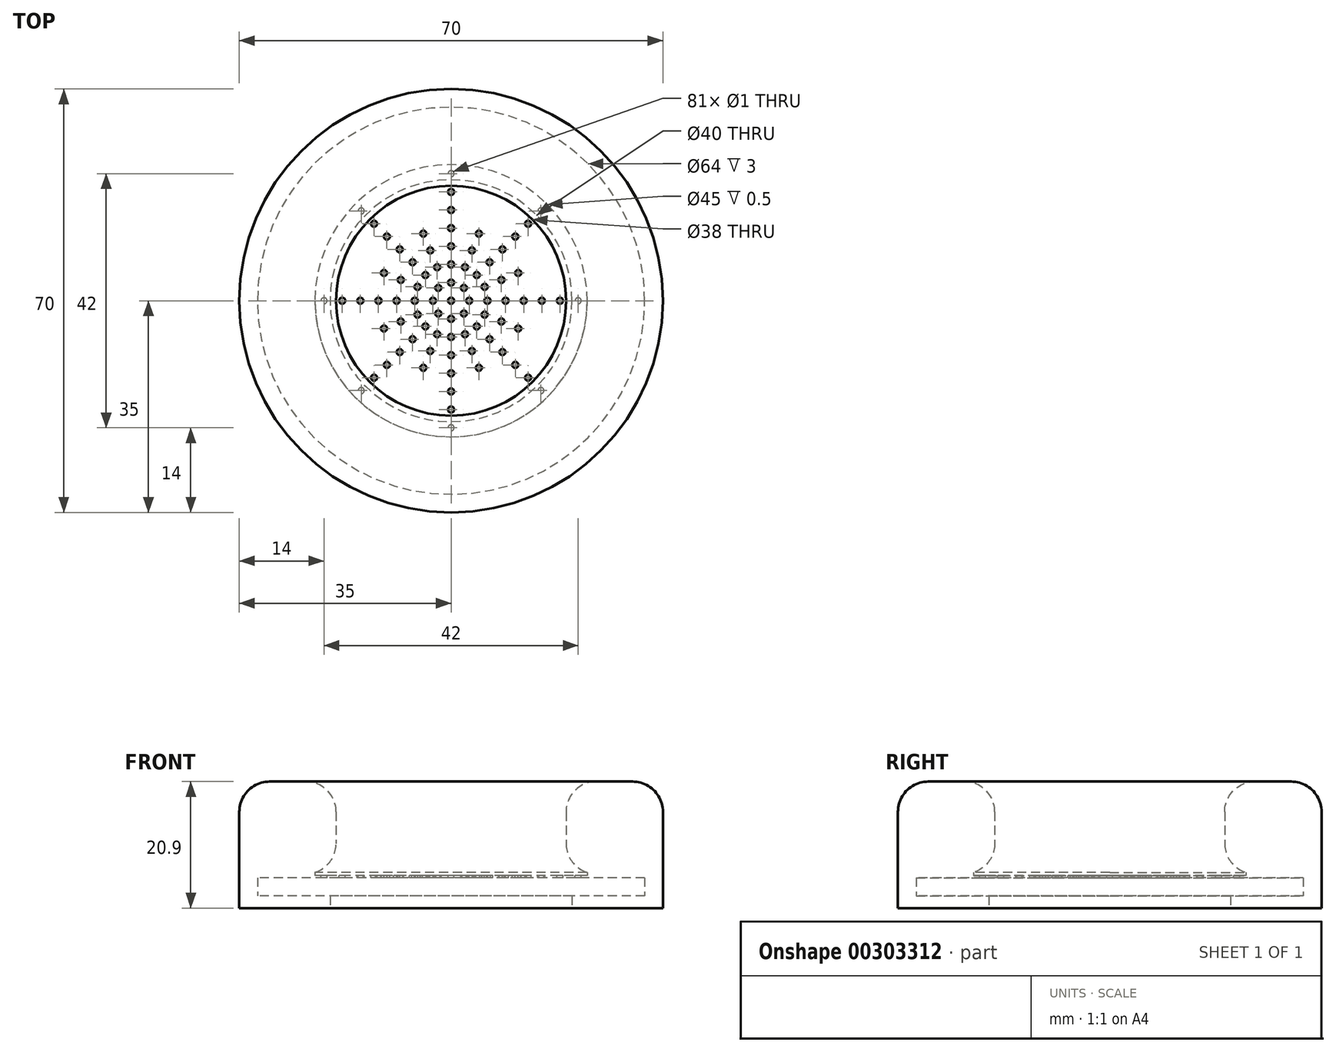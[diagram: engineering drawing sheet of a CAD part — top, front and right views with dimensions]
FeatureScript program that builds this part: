
annotation { "Feature Type Name" : "Feature", "Feature Type Description" : "" }
export const myFeature = defineFeature(function(context is Context, id is Id, definition is map)
    precondition{}
    {
        {
            var Q0;
            Q0=qCreatedBy(makeId("Top.planeOp"),FACE);
            var sketch = newSketch(context, id + "F0", { "sketchPlane" : qUnion([Q0])});
            skCircle(sketch, "E0", {"center": v(0, 0) * mm, "radius": 35 * mm});
            skCircle(sketch, "E1", {"center": v(0, 0) * mm, "radius": 20 * mm});
            skSolve(sketch);
        }
        {
            var Q0;
            Q0=makeQuery(id+"F0.imprint","IMPRINT",FACE,{"disambiguationData":[TD([[makeQuery(id+"F0.imprint","IMPRINT",EDGE,{"derivedFrom":sQuery(id+"F0.wireOp",EDGE,"E0")}),1.0]])]});
            extrude(context, id + "F1", {"entities" : qUnion([Q0]), "depth" : 2 * mm});
        }
        {
            var Q0;
            Q0=makeQuery(id+"F1.opExtrude","CAP_FACE",FACE,{"disambiguationData":[OSD([sQuery(id+"F0.wireOp",EDGE,"E0"),sQuery(id+"F0.wireOp",EDGE,"E1")])],"isStart":false});
            var sketch = newSketch(context, id + "F2", { "sketchPlane" : qUnion([Q0])});
            skCircle(sketch, "E2", {"center": v(0, 0) * mm, "radius": 32 * mm});
            skSolve(sketch);
        }
        {
            var Q0;
            Q0=makeQuery(id+"F2.imprint","IMPRINT",FACE,{"disambiguationData":[TD([[makeQuery(id+"F2.imprint","IMPRINT",EDGE,{"derivedFrom":sQuery(id+"F2.wireOp",EDGE,"E2")}),-1.0]])]});
            extrude(context, id + "F3", {"entities" : qUnion([Q0]), "operationType" : NewBodyOperationType.ADD, "depth" : 3 * mm});
        }
        {
            var Q0;
            Q0=makeQuery(id+"F3.opExtrude","CAP_FACE",FACE,{"disambiguationData":[OSD([sQuery(id+"F0.wireOp",EDGE,"E0"),sQuery(id+"F2.wireOp",EDGE,"E2")])],"isStart":false});
            var sketch = newSketch(context, id + "F4", { "sketchPlane" : qUnion([Q0])});
            skCircle(sketch, "E3", {"center": v(0, 0) * mm, "radius": 35 * mm});
            skSolve(sketch);
        }
        {
            var Q0;
            Q0 = qSketchRegion(id + "F4", true);
            extrude(context, id + "F5", {"entities" : qUnion([Q0]), "operationType" : NewBodyOperationType.ADD, "depth" : 0.4 * mm});
        }
        {
            var Q0;
            Q0=makeQuery(id+"F5.opExtrude","CAP_FACE",FACE,{"disambiguationData":[OSD([sQuery(id+"F4.wireOp",EDGE,"E3")])],"isStart":false});
            var sketch = newSketch(context, id + "F6", { "sketchPlane" : qUnion([Q0])});
            skCircle(sketch, "E4", {"center": v(0, 0) * mm, "radius": 0.5 * mm});
            skCircle(sketch, "E5.1.0.0", {"center": v(3, 0) * mm, "radius": 0.5 * mm});
            skCircle(sketch, "E5.2.0.0", {"center": v(6, 0) * mm, "radius": 0.5 * mm});
            skCircle(sketch, "E5.3.0.0", {"center": v(9, 0) * mm, "radius": 0.5 * mm});
            skCircle(sketch, "E5.4.0.0", {"center": v(12, 0) * mm, "radius": 0.5 * mm});
            skCircle(sketch, "E5.5.0.0", {"center": v(15, 0) * mm, "radius": 0.5 * mm});
            skCircle(sketch, "E5.6.0.0", {"center": v(18, 0) * mm, "radius": 0.5 * mm});
            skCircle(sketch, "E5.7.0.0", {"center": v(21, 0) * mm, "radius": 0.5 * mm});
            skLineSegment(sketch, "E5.direction1", {"start": v(0, 0) * mm, "end": v(3, 0) * mm, "construction": true});
            skCircle(sketch, "E6.1.0", {"center": v(2.12, 2.12) * mm, "radius": 0.5 * mm});
            skCircle(sketch, "E6.1.1", {"center": v(4.24, 4.24) * mm, "radius": 0.5 * mm});
            skCircle(sketch, "E6.1.2", {"center": v(6.36, 6.36) * mm, "radius": 0.5 * mm});
            skCircle(sketch, "E6.1.3", {"center": v(8.49, 8.49) * mm, "radius": 0.5 * mm});
            skCircle(sketch, "E6.1.4", {"center": v(10.6, 10.6) * mm, "radius": 0.5 * mm});
            skCircle(sketch, "E6.1.5", {"center": v(12.73, 12.73) * mm, "radius": 0.5 * mm});
            skCircle(sketch, "E6.1.6", {"center": v(14.85, 14.85) * mm, "radius": 0.5 * mm});
            skCircle(sketch, "E6.2.0", {"center": v(0, 3) * mm, "radius": 0.5 * mm});
            skCircle(sketch, "E6.2.1", {"center": v(0, 6) * mm, "radius": 0.5 * mm});
            skCircle(sketch, "E6.2.2", {"center": v(0, 9) * mm, "radius": 0.5 * mm});
            skCircle(sketch, "E6.2.3", {"center": v(0, 12) * mm, "radius": 0.5 * mm});
            skCircle(sketch, "E6.2.4", {"center": v(0, 15) * mm, "radius": 0.5 * mm});
            skCircle(sketch, "E6.2.5", {"center": v(0, 18) * mm, "radius": 0.5 * mm});
            skCircle(sketch, "E6.2.6", {"center": v(0, 21) * mm, "radius": 0.5 * mm});
            skCircle(sketch, "E6.3.0", {"center": v(-2.12, 2.12) * mm, "radius": 0.5 * mm});
            skCircle(sketch, "E6.3.1", {"center": v(-4.24, 4.24) * mm, "radius": 0.5 * mm});
            skCircle(sketch, "E6.3.2", {"center": v(-6.36, 6.36) * mm, "radius": 0.5 * mm});
            skCircle(sketch, "E6.3.3", {"center": v(-8.49, 8.49) * mm, "radius": 0.5 * mm});
            skCircle(sketch, "E6.3.4", {"center": v(-10.6, 10.6) * mm, "radius": 0.5 * mm});
            skCircle(sketch, "E6.3.5", {"center": v(-12.73, 12.73) * mm, "radius": 0.5 * mm});
            skCircle(sketch, "E6.3.6", {"center": v(-14.85, 14.85) * mm, "radius": 0.5 * mm});
            skCircle(sketch, "E6.4.0", {"center": v(-3, 0) * mm, "radius": 0.5 * mm});
            skCircle(sketch, "E6.4.1", {"center": v(-6, 0) * mm, "radius": 0.5 * mm});
            skCircle(sketch, "E6.4.2", {"center": v(-9, 0) * mm, "radius": 0.5 * mm});
            skCircle(sketch, "E6.4.3", {"center": v(-12, 0) * mm, "radius": 0.5 * mm});
            skCircle(sketch, "E6.4.4", {"center": v(-15, 0) * mm, "radius": 0.5 * mm});
            skCircle(sketch, "E6.4.5", {"center": v(-18, 0) * mm, "radius": 0.5 * mm});
            skCircle(sketch, "E6.4.6", {"center": v(-21, 0) * mm, "radius": 0.5 * mm});
            skCircle(sketch, "E6.5.0", {"center": v(-2.12, -2.12) * mm, "radius": 0.5 * mm});
            skCircle(sketch, "E6.5.1", {"center": v(-4.24, -4.24) * mm, "radius": 0.5 * mm});
            skCircle(sketch, "E6.5.2", {"center": v(-6.36, -6.36) * mm, "radius": 0.5 * mm});
            skCircle(sketch, "E6.5.3", {"center": v(-8.49, -8.49) * mm, "radius": 0.5 * mm});
            skCircle(sketch, "E6.5.4", {"center": v(-10.6, -10.6) * mm, "radius": 0.5 * mm});
            skCircle(sketch, "E6.5.5", {"center": v(-12.73, -12.73) * mm, "radius": 0.5 * mm});
            skCircle(sketch, "E6.5.6", {"center": v(-14.85, -14.85) * mm, "radius": 0.5 * mm});
            skCircle(sketch, "E6.6.0", {"center": v(0, -3) * mm, "radius": 0.5 * mm});
            skCircle(sketch, "E6.6.1", {"center": v(0, -6) * mm, "radius": 0.5 * mm});
            skCircle(sketch, "E6.6.2", {"center": v(0, -9) * mm, "radius": 0.5 * mm});
            skCircle(sketch, "E6.6.3", {"center": v(0, -12) * mm, "radius": 0.5 * mm});
            skCircle(sketch, "E6.6.4", {"center": v(0, -15) * mm, "radius": 0.5 * mm});
            skCircle(sketch, "E6.6.5", {"center": v(0, -18) * mm, "radius": 0.5 * mm});
            skCircle(sketch, "E6.6.6", {"center": v(0, -21) * mm, "radius": 0.5 * mm});
            skCircle(sketch, "E6.7.0", {"center": v(2.12, -2.12) * mm, "radius": 0.5 * mm});
            skCircle(sketch, "E6.7.1", {"center": v(4.24, -4.24) * mm, "radius": 0.5 * mm});
            skCircle(sketch, "E6.7.2", {"center": v(6.36, -6.36) * mm, "radius": 0.5 * mm});
            skCircle(sketch, "E6.7.3", {"center": v(8.49, -8.49) * mm, "radius": 0.5 * mm});
            skCircle(sketch, "E6.7.4", {"center": v(10.6, -10.6) * mm, "radius": 0.5 * mm});
            skCircle(sketch, "E6.7.5", {"center": v(12.73, -12.73) * mm, "radius": 0.5 * mm});
            skCircle(sketch, "E6.7.6", {"center": v(14.85, -14.85) * mm, "radius": 0.5 * mm});
            skCircle(sketch, "E7.1.0", {"center": v(5.54, 2.3) * mm, "radius": 0.5 * mm});
            skCircle(sketch, "E7.1.1", {"center": v(8.31, 3.44) * mm, "radius": 0.5 * mm});
            skCircle(sketch, "E7.1.2", {"center": v(11.09, 4.6) * mm, "radius": 0.5 * mm});
            skCircle(sketch, "E7.3.0", {"center": v(2.3, 5.54) * mm, "radius": 0.5 * mm});
            skCircle(sketch, "E7.3.1", {"center": v(3.44, 8.31) * mm, "radius": 0.5 * mm});
            skCircle(sketch, "E7.3.2", {"center": v(4.6, 11.09) * mm, "radius": 0.5 * mm});
            skCircle(sketch, "E7.5.0", {"center": v(-2.3, 5.54) * mm, "radius": 0.5 * mm});
            skCircle(sketch, "E7.5.1", {"center": v(-3.44, 8.31) * mm, "radius": 0.5 * mm});
            skCircle(sketch, "E7.5.2", {"center": v(-4.6, 11.09) * mm, "radius": 0.5 * mm});
            skCircle(sketch, "E7.7.0", {"center": v(-5.54, 2.3) * mm, "radius": 0.5 * mm});
            skCircle(sketch, "E7.7.1", {"center": v(-8.31, 3.44) * mm, "radius": 0.5 * mm});
            skCircle(sketch, "E7.7.2", {"center": v(-11.09, 4.6) * mm, "radius": 0.5 * mm});
            skCircle(sketch, "E7.9.0", {"center": v(-5.54, -2.3) * mm, "radius": 0.5 * mm});
            skCircle(sketch, "E7.9.1", {"center": v(-8.31, -3.44) * mm, "radius": 0.5 * mm});
            skCircle(sketch, "E7.9.2", {"center": v(-11.09, -4.6) * mm, "radius": 0.5 * mm});
            skCircle(sketch, "E7.11.0", {"center": v(-2.3, -5.54) * mm, "radius": 0.5 * mm});
            skCircle(sketch, "E7.11.1", {"center": v(-3.44, -8.31) * mm, "radius": 0.5 * mm});
            skCircle(sketch, "E7.11.2", {"center": v(-4.6, -11.09) * mm, "radius": 0.5 * mm});
            skCircle(sketch, "E7.13.0", {"center": v(2.3, -5.54) * mm, "radius": 0.5 * mm});
            skCircle(sketch, "E7.13.1", {"center": v(3.44, -8.31) * mm, "radius": 0.5 * mm});
            skCircle(sketch, "E7.13.2", {"center": v(4.6, -11.09) * mm, "radius": 0.5 * mm});
            skCircle(sketch, "E7.15.0", {"center": v(5.54, -2.3) * mm, "radius": 0.5 * mm});
            skCircle(sketch, "E7.15.1", {"center": v(8.31, -3.44) * mm, "radius": 0.5 * mm});
            skCircle(sketch, "E7.15.2", {"center": v(11.09, -4.6) * mm, "radius": 0.5 * mm});
            skSolve(sketch);
        }
        {
            var Q0;
            Q0 = qSketchRegion(id + "F6", true);
            extrude(context, id + "F7", {"entities" : qUnion([Q0]), "operationType" : NewBodyOperationType.REMOVE, "oppositeDirection" : true, "depth" : 1 * mm});
        }
        {
            var Q0;
            Q0=makeQuery(id+"F5.opExtrude","CAP_FACE",FACE,{"disambiguationData":[OSD([sQuery(id+"F4.wireOp",EDGE,"E3")])],"isStart":false});
            var sketch = newSketch(context, id + "F8", { "sketchPlane" : qUnion([Q0])});
            skCircle(sketch, "E8", {"center": v(0, 0) * mm, "radius": 22.5 * mm});
            skSolve(sketch);
        }
        {
            var Q0;
            Q0=makeQuery(id+"F8.imprint","IMPRINT",FACE,{"disambiguationData":[TD([[makeQuery(id+"F8.imprint","IMPRINT",EDGE,{"derivedFrom":sQuery(id+"F8.wireOp",EDGE,"E8")}),-1.0]])]});
            extrude(context, id + "F9", {"entities" : qUnion([Q0]), "operationType" : NewBodyOperationType.ADD, "depth" : 0.5 * mm});
        }
        {
            var Q0;
            Q0=makeQuery(id+"F9.opExtrude","CAP_FACE",FACE,{"disambiguationData":[OSD([sQuery(id+"F4.wireOp",EDGE,"E3"),sQuery(id+"F8.wireOp",EDGE,"E8")])],"isStart":false});
            var sketch = newSketch(context, id + "F10", { "sketchPlane" : qUnion([Q0])});
            skCircle(sketch, "E9", {"center": v(0, 0) * mm, "radius": 19 * mm});
            skSolve(sketch);
        }
        {
            var Q0;
            Q0=makeQuery(id+"F10.imprint","IMPRINT",FACE,{"disambiguationData":[TD([[makeQuery(id+"F10.imprint","IMPRINT",EDGE,{"derivedFrom":sQuery(id+"F10.wireOp",EDGE,"E9")}),-1.0]])]});
            var Q1;
            Q1=makeQuery(id+"F10.imprint","IMPRINT",FACE,{"disambiguationData":[TD([[makeQuery(id+"F10.imprint","IMPRINT",EDGE,{"derivedFrom":makeQuery(id+"F9.opExtrude","CAP_EDGE",EDGE,{"disambiguationData":[OSD([sQuery(id+"F8.wireOp",EDGE,"E8")])],"isStart":false})}),-1.0]])]});
            extrude(context, id + "F11", {"entities" : qUnion([Q0, Q1]), "operationType" : NewBodyOperationType.ADD, "depth" : 15 * mm});
        }
        {
            var Q0;
            Q0=makeQuery(id+"F11.opExtrude","CAP_FACE",FACE,{"disambiguationData":[OSD([sQuery(id+"F4.wireOp",EDGE,"E3"),sQuery(id+"F10.wireOp",EDGE,"E9")])],"isStart":false});
            var Q1;
            Q1=makeQuery(id+"F11.opExtrude","SWEPT_FACE",FACE,{"disambiguationData":[OSD([sQuery(id+"F10.wireOp",EDGE,"E9")])]});
            fillet(context, id + "F12", {"entities" : qUnion([Q0, Q1]), "radius" : 5 * mm, "tangentPropagation" : true, "allowEdgeOverflow" : false});
        }
    });
